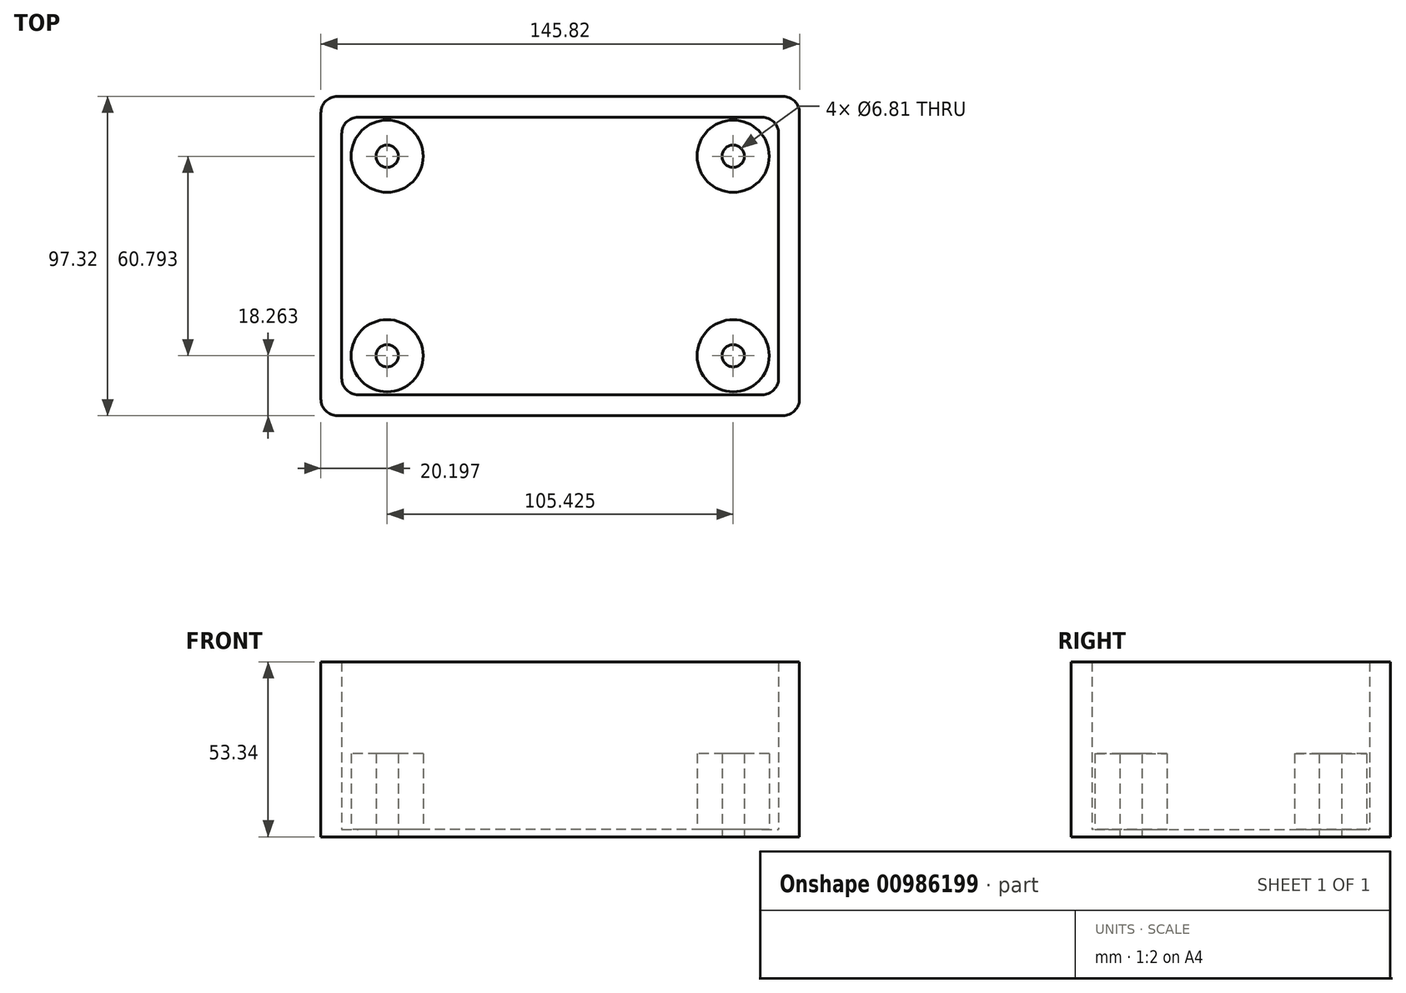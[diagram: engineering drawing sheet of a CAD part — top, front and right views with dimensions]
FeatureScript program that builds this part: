
annotation { "Feature Type Name" : "Feature", "Feature Type Description" : "" }
export const myFeature = defineFeature(function(context is Context, id is Id, definition is map)
    precondition{}
    {
        {
            var Q0;
            Q0=qCreatedBy(makeId("Top.planeOp"),FACE);
            var sketch = newSketch(context, id + "F0", { "sketchPlane" : qUnion([Q0])});
            skLineSegment(sketch, "E0.bottom", {"start": v(66.56, -42.3) * mm, "end": v(-66.56, -42.3) * mm});
            skLineSegment(sketch, "E0.top", {"start": v(66.56, 42.3) * mm, "end": v(-66.56, 42.3) * mm});
            skLineSegment(sketch, "E0.left", {"start": v(66.56, -42.3) * mm, "end": v(66.56, 42.3) * mm});
            skLineSegment(sketch, "E0.right", {"start": v(-66.56, -42.3) * mm, "end": v(-66.56, 42.3) * mm});
            skPoint(sketch, "E0.middle", {"position": v(0, 0) * mm});
            skLineSegment(sketch, "E1.0", {"start": v(72.9, 48.66) * mm, "end": v(-72.9, 48.66) * mm});
            skLineSegment(sketch, "E1.1", {"start": v(72.9, -48.66) * mm, "end": v(72.9, 48.66) * mm});
            skLineSegment(sketch, "E1.2", {"start": v(72.9, -48.66) * mm, "end": v(-72.9, -48.66) * mm});
            skLineSegment(sketch, "E1.3", {"start": v(-72.9, -48.66) * mm, "end": v(-72.9, 48.66) * mm});
            skLineSegment(sketch, "E2.bottom", {"start": v(52.71, -30.4) * mm, "end": v(-52.71, -30.4) * mm, "construction": true});
            skLineSegment(sketch, "E2.top", {"start": v(52.71, 30.4) * mm, "end": v(-52.71, 30.4) * mm, "construction": true});
            skLineSegment(sketch, "E2.left", {"start": v(52.71, -30.4) * mm, "end": v(52.71, 30.4) * mm, "construction": true});
            skLineSegment(sketch, "E2.right", {"start": v(-52.71, -30.4) * mm, "end": v(-52.71, 30.4) * mm, "construction": true});
            skCircle(sketch, "E3", {"center": v(-52.71, 30.4) * mm, "radius": 10.99 * mm});
            skCircle(sketch, "E4", {"center": v(-52.71, -30.4) * mm, "radius": 10.99 * mm});
            skCircle(sketch, "E5", {"center": v(52.71, -30.4) * mm, "radius": 10.99 * mm});
            skCircle(sketch, "E6", {"center": v(52.71, 30.4) * mm, "radius": 10.99 * mm});
            skCircle(sketch, "E7", {"center": v(-52.71, 30.4) * mm, "radius": 3.4 * mm});
            skCircle(sketch, "E8", {"center": v(-52.71, -30.4) * mm, "radius": 3.4 * mm});
            skCircle(sketch, "E9", {"center": v(52.71, 30.4) * mm, "radius": 3.4 * mm});
            skCircle(sketch, "E10", {"center": v(52.71, -30.4) * mm, "radius": 3.4 * mm});
            skSolve(sketch);
        }
        {
            var Q0;
            Q0 = qSketchRegion(id + "F0", true);
            extrude(context, id + "F1", {"entities" : qUnion([Q0]), "depth" : 25.4 * mm, "offsetDistance" : 25.4 * mm});
        }
        {
            var Q0;
            Q0=makeQuery(id+"F0.imprint","IMPRINT",FACE,{"disambiguationData":[TD([[makeQuery(id+"F0.imprint","IMPRINT",EDGE,{"derivedFrom":sQuery(id+"F0.wireOp",EDGE,"E0.bottom")}),-1.0]])]});
            extrude(context, id + "F2", {"entities" : qUnion([Q0]), "operationType" : NewBodyOperationType.ADD, "depth" : 2.3 * mm, "offsetDistance" : 25.4 * mm});
        }
        {
            var Q0;
            Q0=makeQuery(id+"F0.imprint","IMPRINT",FACE,{"disambiguationData":[TD([[makeQuery(id+"F0.imprint","IMPRINT",EDGE,{"derivedFrom":sQuery(id+"F0.wireOp",EDGE,"E3")}),1.0]])]});
            extrude(context, id + "F3", {"entities" : qUnion([Q0]), "operationType" : NewBodyOperationType.ADD, "depth" : 25.4 * mm, "offsetDistance" : 25.4 * mm});
        }
        {
            var Q0;
            Q0=makeQuery(id+"F0.imprint","IMPRINT",FACE,{"disambiguationData":[TD([[makeQuery(id+"F0.imprint","IMPRINT",EDGE,{"derivedFrom":sQuery(id+"F0.wireOp",EDGE,"E6")}),1.0]])]});
            extrude(context, id + "F4", {"entities" : qUnion([Q0]), "operationType" : NewBodyOperationType.ADD, "depth" : 25.4 * mm, "offsetDistance" : 25.4 * mm});
        }
        {
            var Q0;
            Q0=makeQuery(id+"F0.imprint","IMPRINT",FACE,{"disambiguationData":[TD([[makeQuery(id+"F0.imprint","IMPRINT",EDGE,{"derivedFrom":sQuery(id+"F0.wireOp",EDGE,"E4")}),1.0]])]});
            var Q1;
            Q1=makeQuery(id+"F0.imprint","IMPRINT",FACE,{"disambiguationData":[TD([[makeQuery(id+"F0.imprint","IMPRINT",EDGE,{"derivedFrom":sQuery(id+"F0.wireOp",EDGE,"E5")}),1.0]])]});
            extrude(context, id + "F5", {"entities" : qUnion([Q0, Q1]), "operationType" : NewBodyOperationType.ADD, "depth" : 25.4 * mm, "offsetDistance" : 25.4 * mm});
        }
        {
            var Q0;
            Q0=makeQuery(id+"F1.opExtrude","SWEPT_EDGE",EDGE,{"disambiguationData":[OSD([sQuery(id+"F0.wireOp",EDGE,"E1.2"),sQuery(id+"F0.wireOp",EDGE,"E1.3")])]});
            var Q1;
            Q1=makeQuery(id+"F1.opExtrude","SWEPT_EDGE",EDGE,{"disambiguationData":[OSD([sQuery(id+"F0.wireOp",EDGE,"E1.1"),sQuery(id+"F0.wireOp",EDGE,"E1.2")])]});
            fillet(context, id + "F6", {"entities" : qUnion([Q0, Q1]), "radius" : 5.08 * mm, "tangentPropagation" : true, "allowEdgeOverflow" : false});
        }
        {
            var Q0;
            Q0=makeQuery(id+"F1.opExtrude","SWEPT_EDGE",EDGE,{"disambiguationData":[OSD([sQuery(id+"F0.wireOp",EDGE,"E0.top"),sQuery(id+"F0.wireOp",EDGE,"E0.right")])]});
            fillet(context, id + "F7", {"entities" : qUnion([Q0]), "radius" : 5.08 * mm, "tangentPropagation" : true, "allowEdgeOverflow" : false});
        }
        {
            var Q0;
            Q0=makeQuery(id+"F1.opExtrude","SWEPT_EDGE",EDGE,{"disambiguationData":[OSD([sQuery(id+"F0.wireOp",EDGE,"E1.0"),sQuery(id+"F0.wireOp",EDGE,"E1.1")])]});
            fillet(context, id + "F8", {"entities" : qUnion([Q0]), "radius" : 5.08 * mm, "tangentPropagation" : true, "allowEdgeOverflow" : false});
        }
        {
            var Q0;
            Q0=makeQuery(id+"F1.opExtrude","SWEPT_EDGE",EDGE,{"disambiguationData":[OSD([sQuery(id+"F0.wireOp",EDGE,"E1.0"),sQuery(id+"F0.wireOp",EDGE,"E1.3")])]});
            fillet(context, id + "F9", {"entities" : qUnion([Q0]), "radius" : 5.08 * mm, "tangentPropagation" : true, "allowEdgeOverflow" : false});
        }
        {
            var Q0;
            Q0=makeQuery(id+"F1.opExtrude","SWEPT_EDGE",EDGE,{"disambiguationData":[OSD([sQuery(id+"F0.wireOp",EDGE,"E0.bottom"),sQuery(id+"F0.wireOp",EDGE,"E0.left")])]});
            fillet(context, id + "F10", {"entities" : qUnion([Q0]), "radius" : 5.08 * mm, "tangentPropagation" : true, "allowEdgeOverflow" : false});
        }
        {
            var Q0;
            Q0=makeQuery(id+"F1.opExtrude","SWEPT_EDGE",EDGE,{"disambiguationData":[OSD([sQuery(id+"F0.wireOp",EDGE,"E0.top"),sQuery(id+"F0.wireOp",EDGE,"E0.left")])]});
            fillet(context, id + "F11", {"entities" : qUnion([Q0]), "radius" : 5.08 * mm, "tangentPropagation" : true, "allowEdgeOverflow" : false});
        }
        {
            var Q0;
            Q0=makeQuery(id+"F1.opExtrude","SWEPT_EDGE",EDGE,{"disambiguationData":[OSD([sQuery(id+"F0.wireOp",EDGE,"E0.bottom"),sQuery(id+"F0.wireOp",EDGE,"E0.right")])]});
            fillet(context, id + "F12", {"entities" : qUnion([Q0]), "radius" : 5.08 * mm, "tangentPropagation" : true, "allowEdgeOverflow" : false});
        }
        {
            var Q0;
            Q0=makeQuery(id+"F1.opExtrude","CAP_FACE",FACE,{"disambiguationData":[OSD([sQuery(id+"F0.wireOp",EDGE,"E0.bottom"),sQuery(id+"F0.wireOp",EDGE,"E0.top"),sQuery(id+"F0.wireOp",EDGE,"E0.left"),sQuery(id+"F0.wireOp",EDGE,"E0.right"),sQuery(id+"F0.wireOp",EDGE,"E1.0"),sQuery(id+"F0.wireOp",EDGE,"E1.1"),sQuery(id+"F0.wireOp",EDGE,"E1.2"),sQuery(id+"F0.wireOp",EDGE,"E1.3")])],"isStart":false});
            extrude(context, id + "F13", {"entities" : qUnion([Q0]), "operationType" : NewBodyOperationType.ADD, "depth" : 27.94 * mm, "offsetDistance" : 25.4 * mm});
        }
    });
